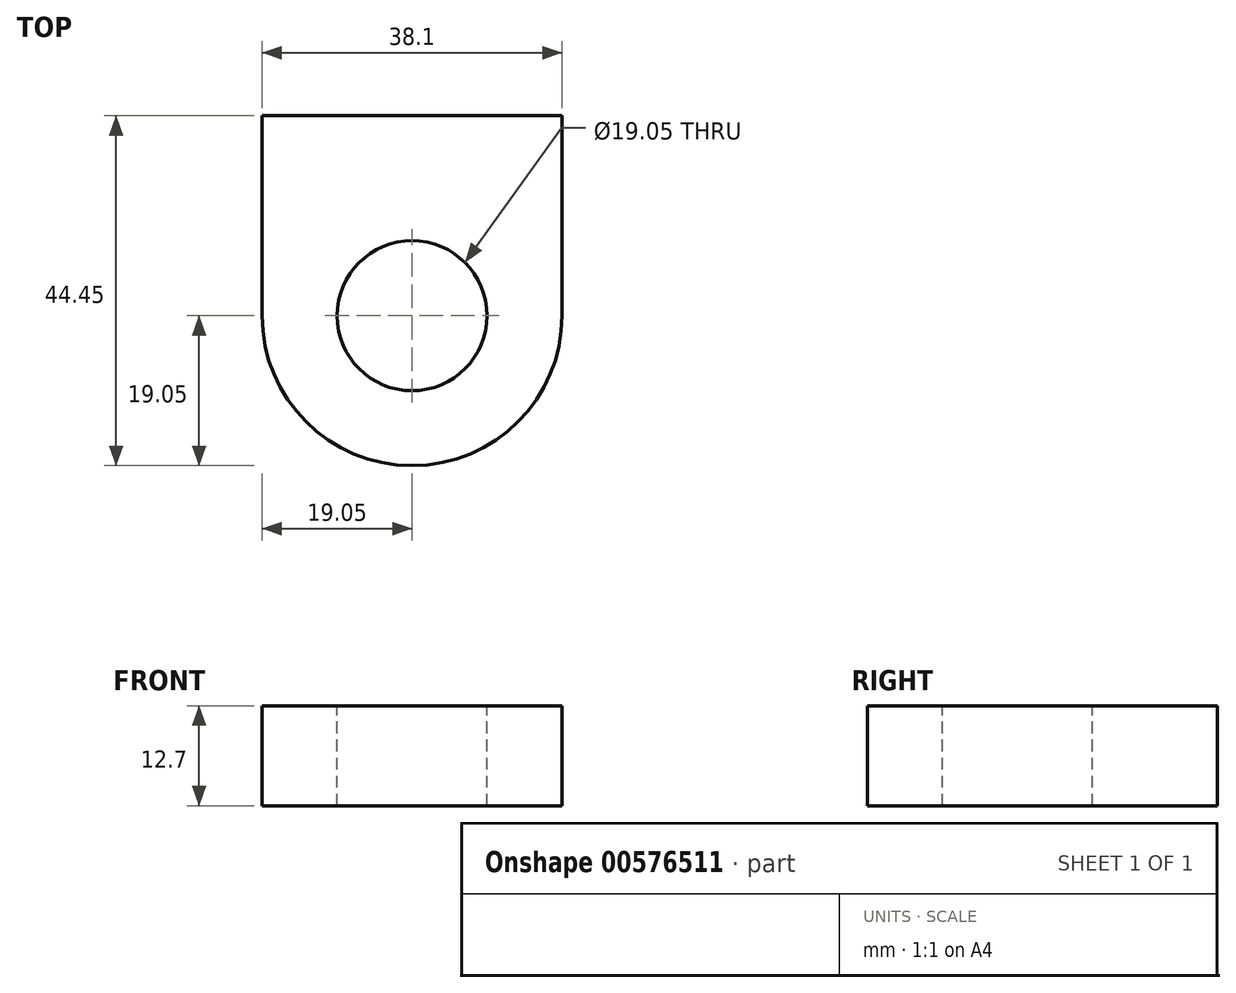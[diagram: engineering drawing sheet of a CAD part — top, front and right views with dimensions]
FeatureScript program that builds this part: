
annotation { "Feature Type Name" : "Feature", "Feature Type Description" : "" }
export const myFeature = defineFeature(function(context is Context, id is Id, definition is map)
    precondition{}
    {
        {
            var Q0;
            Q0=qCreatedBy(makeId("Top.planeOp"),FACE);
            var sketch = newSketch(context, id + "F0", { "sketchPlane" : qUnion([Q0])});
            skLineSegment(sketch, "E0.bottom", {"start": v(-19.05, -12.7) * mm, "end": v(19.05, -12.7) * mm});
            skLineSegment(sketch, "E0.top", {"start": v(-19.05, 12.7) * mm, "end": v(19.05, 12.7) * mm});
            skLineSegment(sketch, "E0.left", {"start": v(-19.05, -12.7) * mm, "end": v(-19.05, 12.7) * mm});
            skLineSegment(sketch, "E0.right", {"start": v(19.05, -12.7) * mm, "end": v(19.05, 12.7) * mm});
            skPoint(sketch, "E0.middle", {"position": v(0, 0) * mm});
            skArc(sketch, "E1", {"start": v(-19.05, -12.7) * mm, "mid": v(0, -31.75) * mm, "end": v(19.05, -12.7) * mm});
            skSolve(sketch);
        }
        {
            var Q0;
            Q0=makeQuery(id+"F0.imprint","IMPRINT",FACE,{"disambiguationData":[TD([[makeQuery(id+"F0.imprint","IMPRINT",EDGE,{"derivedFrom":sQuery(id+"F0.wireOp",EDGE,"E0.bottom")}),1.0]])]});
            var Q1;
            Q1=makeQuery(id+"F0.imprint","IMPRINT",FACE,{"disambiguationData":[TD([[makeQuery(id+"F0.imprint","IMPRINT",EDGE,{"derivedFrom":sQuery(id+"F0.wireOp",EDGE,"E0.bottom")}),-1.0]])]});
            extrude(context, id + "F1", {"entities" : qUnion([Q0, Q1]), "depth" : 12.7 * mm, "offsetDistance" : 25.4 * mm});
        }
        {
            var Q0;
            Q0=makeQuery(id+"F1.opExtrude","CAP_FACE",FACE,{"disambiguationData":[OSD([sQuery(id+"F0.wireOp",EDGE,"E0.top"),sQuery(id+"F0.wireOp",EDGE,"E0.left"),sQuery(id+"F0.wireOp",EDGE,"E0.right"),sQuery(id+"F0.wireOp",EDGE,"E1")])],"isStart":false});
            var sketch = newSketch(context, id + "F2", { "sketchPlane" : qUnion([Q0])});
            skCircle(sketch, "E2", {"center": v(0, -12.7) * mm, "radius": 9.53 * mm});
            skSolve(sketch);
        }
        {
            var Q0;
            Q0=makeQuery(id+"F2.imprint","IMPRINT",FACE,{"disambiguationData":[TD([[makeQuery(id+"F2.imprint","IMPRINT",EDGE,{"derivedFrom":sQuery(id+"F2.wireOp",EDGE,"E2")}),1.0]])]});
            extrude(context, id + "F3", {"entities" : qUnion([Q0]), "operationType" : NewBodyOperationType.REMOVE, "endBound" : BoundingType.THROUGH_ALL, "oppositeDirection" : true, "depth" : 25.4 * mm, "offsetDistance" : 25.4 * mm});
        }
    });
